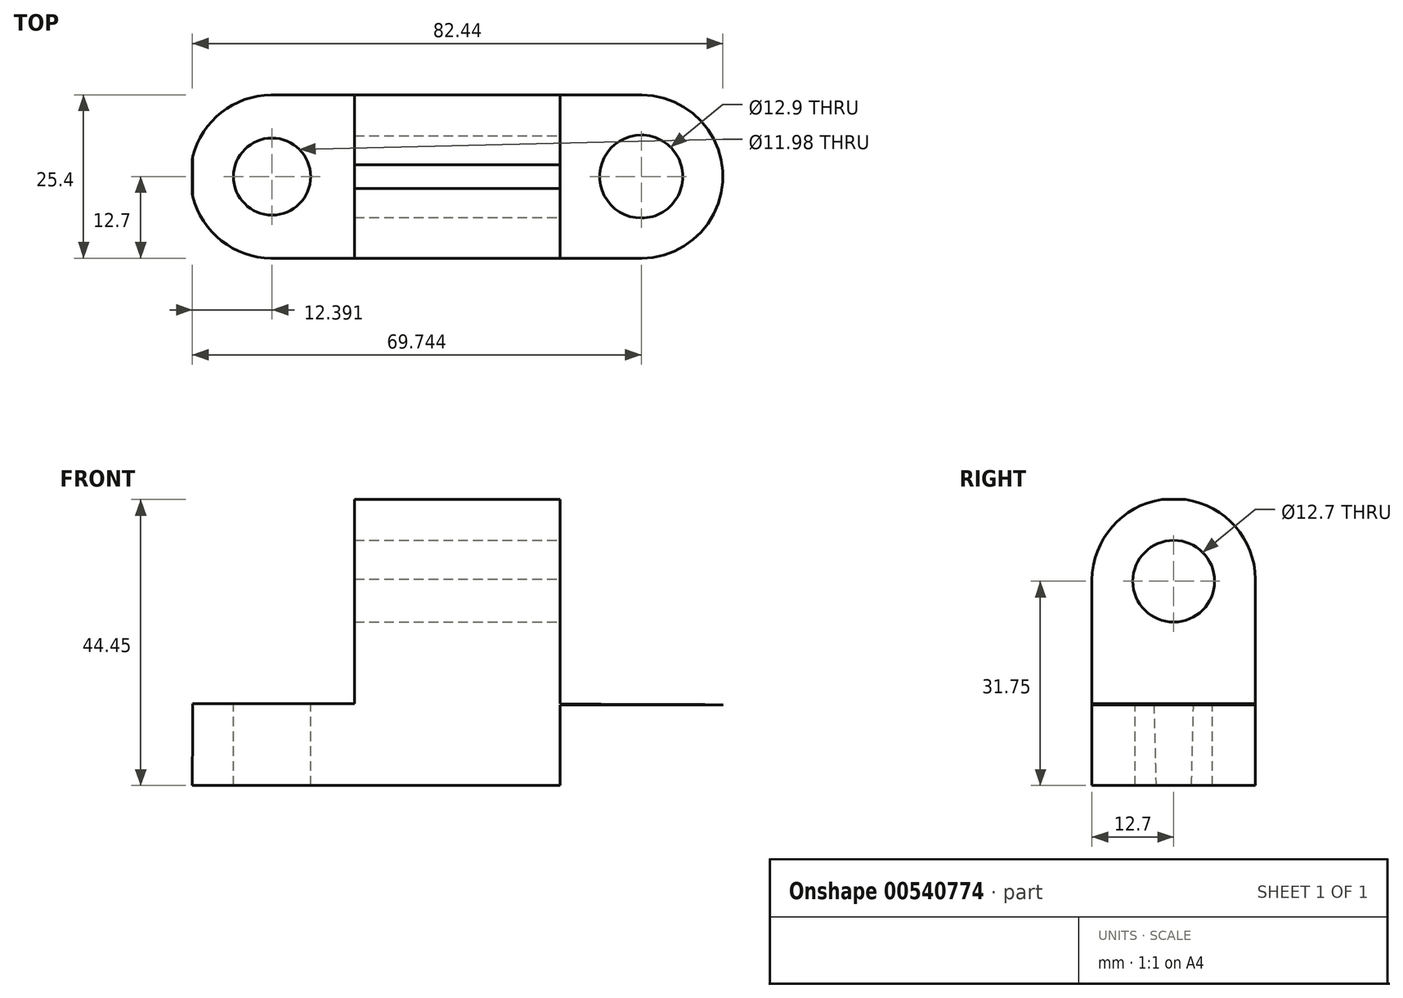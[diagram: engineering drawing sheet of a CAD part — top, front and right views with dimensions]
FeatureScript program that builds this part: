
annotation { "Feature Type Name" : "Feature", "Feature Type Description" : "" }
export const myFeature = defineFeature(function(context is Context, id is Id, definition is map)
    precondition{}
    {
        {
            var Q0;
            Q0=qCreatedBy(makeId("Front.planeOp"),FACE);
            var sketch = newSketch(context, id + "F0", { "sketchPlane" : qUnion([Q0])});
            skLineSegment(sketch, "E0", {"start": v(-37.24, 0) * mm, "end": v(45.57, 0) * mm});
            skLineSegment(sketch, "E1", {"start": v(45.57, 0) * mm, "end": v(45.57, 44.45) * mm});
            skLineSegment(sketch, "E2", {"start": v(45.57, 44.45) * mm, "end": v(-36.98, 44.45) * mm});
            skLineSegment(sketch, "E3", {"start": v(-36.98, 44.45) * mm, "end": v(-37.24, 0) * mm});
            skSolve(sketch);
        }
        {
            var Q0;
            Q0=makeQuery(id+"F0.imprint","IMPRINT",FACE,{"disambiguationData":[TD([[makeQuery(id+"F0.imprint","IMPRINT",EDGE,{"derivedFrom":sQuery(id+"F0.wireOp",EDGE,"E0")}),1.0]])]});
            extrude(context, id + "F1", {"entities" : qUnion([Q0]), "depth" : 25.4 * mm, "offsetDistance" : 25.4 * mm});
        }
        {
            var Q0;
            Q0=makeQuery(id+"F1.opExtrude","CAP_FACE",FACE,{"disambiguationData":[OSD([sQuery(id+"F0.wireOp",EDGE,"E0"),sQuery(id+"F0.wireOp",EDGE,"E1"),sQuery(id+"F0.wireOp",EDGE,"E2"),sQuery(id+"F0.wireOp",EDGE,"E3")])],"isStart":false});
            var sketch = newSketch(context, id + "F2", { "sketchPlane" : qUnion([Q0])});
            skLineSegment(sketch, "E4", {"start": v(45.57, 12.55) * mm, "end": v(20.17, 12.7) * mm});
            skLineSegment(sketch, "E5", {"start": v(20.17, 12.7) * mm, "end": v(20.17, 44.45) * mm});
            skLineSegment(sketch, "E6", {"start": v(-11.76, 12.7) * mm, "end": v(-11.76, 44.45) * mm});
            skLineSegment(sketch, "E7", {"start": v(20.17, 44.45) * mm, "end": v(45.57, 44.45) * mm});
            skLineSegment(sketch, "E8", {"start": v(45.57, 44.45) * mm, "end": v(45.57, 12.55) * mm});
            skLineSegment(sketch, "E9", {"start": v(-11.76, 44.45) * mm, "end": v(-36.98, 44.45) * mm});
            skLineSegment(sketch, "E10", {"start": v(-11.76, 12.7) * mm, "end": v(-37.16, 12.7) * mm});
            skLineSegment(sketch, "E11", {"start": v(-37.16, 12.7) * mm, "end": v(-36.98, 44.45) * mm});
            skSolve(sketch);
        }
        {
            var Q0;
            Q0=makeQuery(id+"F2.imprint","IMPRINT",FACE,{"disambiguationData":[TD([[makeQuery(id+"F2.imprint","IMPRINT",EDGE,{"derivedFrom":sQuery(id+"F2.wireOp",EDGE,"E6")}),1.0]])]});
            var Q1;
            Q1=makeQuery(id+"F2.imprint","IMPRINT",FACE,{"disambiguationData":[TD([[makeQuery(id+"F2.imprint","IMPRINT",EDGE,{"derivedFrom":sQuery(id+"F2.wireOp",EDGE,"E4")}),-1.0]])]});
            extrude(context, id + "F3", {"entities" : qUnion([Q0, Q1]), "operationType" : NewBodyOperationType.REMOVE, "oppositeDirection" : true, "depth" : 25.4 * mm, "offsetDistance" : 25.4 * mm});
        }
        {
            var Q0;
            Q0=makeQuery(id+"F3.boolean.opBoolean","COPY",FACE,{"derivedFrom":makeQuery(id+"F3.opExtrude","SWEPT_FACE",FACE,{"disambiguationData":[OSD([sQuery(id+"F2.wireOp",EDGE,"E5")])]})});
            var sketch = newSketch(context, id + "F4", { "sketchPlane" : qUnion([Q0])});
            skCircle(sketch, "E12", {"center": v(-12.7, 31.75) * mm, "radius": 6.35 * mm});
            skArc(sketch, "E13", {"start": v(0, 32.06) * mm, "mid": v(-12.83, 44.58) * mm, "end": v(-25.4, 31.8) * mm});
            skLineSegment(sketch, "E14", {"start": v(-25.4, 31.8) * mm, "end": v(-25.4, 44.45) * mm});
            skLineSegment(sketch, "E15", {"start": v(-25.4, 44.45) * mm, "end": v(0, 44.45) * mm});
            skLineSegment(sketch, "E16", {"start": v(0, 44.45) * mm, "end": v(0, 32.06) * mm});
            skSolve(sketch);
        }
        {
            var Q0;
            Q0=makeQuery(id+"F4.imprint","IMPRINT",FACE,{"disambiguationData":[TD([[makeQuery(id+"F4.imprint","IMPRINT",EDGE,{"derivedFrom":sQuery(id+"F4.wireOp",EDGE,"E12")}),1.0]])]});
            var Q1;
            {var subQ0=sQuery(id+"F4.wireOp",EDGE,"E14");var subQ1=sQuery(id+"F4.wireOp",EDGE,"E13");var subQ2=makeQuery(id+"F4.imprint","INTERSECT",VERTEX,{"derivedFrom":[subQ1,subQ0]});Q1=makeQuery(id+"F4.imprint","IMPRINT",FACE,{"disambiguationData":[TD([[makeQuery(id+"F4.imprint","IMPRINT",EDGE,{"disambiguationData":[TD([[subQ2,1.0]])],"derivedFrom":subQ1}),-1.0]])]});}
            var Q2;
            {var subQ0=sQuery(id+"F4.wireOp",EDGE,"E16");Q2=makeQuery(id+"F4.imprint","IMPRINT",FACE,{"disambiguationData":[TD([[makeQuery(id+"F4.imprint","IMPRINT",EDGE,{"derivedFrom":subQ0}),1.0]])]});}
            extrude(context, id + "F5", {"entities" : qUnion([Q0, Q1, Q2]), "operationType" : NewBodyOperationType.REMOVE, "oppositeDirection" : true, "depth" : 38.1 * mm, "offsetDistance" : 25.4 * mm});
        }
        {
            var Q0;
            Q0=makeQuery(id+"F3.boolean.opBoolean","COPY",FACE,{"derivedFrom":makeQuery(id+"F3.opExtrude","SWEPT_FACE",FACE,{"disambiguationData":[OSD([sQuery(id+"F2.wireOp",EDGE,"E4")])]})});
            var sketch = newSketch(context, id + "F6", { "sketchPlane" : qUnion([Q0])});
            skArc(sketch, "E17", {"start": v(32.8, -25.4) * mm, "mid": v(45.4, -12.7) * mm, "end": v(32.8, 0) * mm});
            skLineSegment(sketch, "E18", {"start": v(32.8, 0) * mm, "end": v(45.5, 0) * mm});
            skLineSegment(sketch, "E19", {"start": v(45.5, 0) * mm, "end": v(45.5, -25.4) * mm});
            skLineSegment(sketch, "E20", {"start": v(45.5, -25.4) * mm, "end": v(32.8, -25.4) * mm});
            skCircle(sketch, "E21", {"center": v(32.69, -12.7) * mm, "radius": 6.45 * mm});
            skSolve(sketch);
        }
        {
            var Q0;
            Q0=makeQuery(id+"F6.imprint","IMPRINT",FACE,{"disambiguationData":[TD([[makeQuery(id+"F6.imprint","IMPRINT",EDGE,{"derivedFrom":sQuery(id+"F6.wireOp",EDGE,"E17")}),-1.0]])]});
            var Q1;
            Q1=makeQuery(id+"F6.imprint","IMPRINT",FACE,{"disambiguationData":[TD([[makeQuery(id+"F6.imprint","IMPRINT",EDGE,{"derivedFrom":sQuery(id+"F6.wireOp",EDGE,"E21")}),1.0]])]});
            extrude(context, id + "F7", {"entities" : qUnion([Q0, Q1]), "operationType" : NewBodyOperationType.REMOVE, "oppositeDirection" : true, "depth" : 12.7 * mm, "offsetDistance" : 25.4 * mm});
        }
        {
            var Q0;
            Q0=makeQuery(id+"F1.opExtrude","SWEPT_FACE",FACE,{"disambiguationData":[OSD([sQuery(id+"F0.wireOp",EDGE,"E1")])]});
            extrude(context, id + "F8", {"entities" : qUnion([Q0]), "operationType" : NewBodyOperationType.REMOVE, "oppositeDirection" : true, "depth" : 25.4 * mm, "offsetDistance" : 25.4 * mm});
        }
        {
            var Q0;
            Q0=makeQuery(id+"F3.boolean.opBoolean","COPY",FACE,{"derivedFrom":makeQuery(id+"F3.opExtrude","SWEPT_FACE",FACE,{"disambiguationData":[OSD([sQuery(id+"F2.wireOp",EDGE,"E10")])]})});
            var sketch = newSketch(context, id + "F9", { "sketchPlane" : qUnion([Q0])});
            skArc(sketch, "E22", {"start": v(-24.46, 0) * mm, "mid": v(-37.29, -12.7) * mm, "end": v(-24.46, -25.4) * mm});
            skCircle(sketch, "E23", {"center": v(-24.59, -12.7) * mm, "radius": 5.99 * mm});
            skLineSegment(sketch, "E24", {"start": v(-24.46, 0) * mm, "end": v(-37.16, 0) * mm});
            skLineSegment(sketch, "E25", {"start": v(-37.16, 0) * mm, "end": v(-37.16, -25.4) * mm});
            skLineSegment(sketch, "E26", {"start": v(-37.16, -25.4) * mm, "end": v(-24.46, -25.4) * mm});
            skSolve(sketch);
        }
        {
            var Q0;
            {var subQ0=sQuery(id+"F9.wireOp",EDGE,"E24");var subQ1=sQuery(id+"F9.wireOp",EDGE,"E22");var subQ2=makeQuery(id+"F9.imprint","INTERSECT",VERTEX,{"derivedFrom":[subQ1,subQ0]});Q0=makeQuery(id+"F9.imprint","IMPRINT",FACE,{"disambiguationData":[TD([[makeQuery(id+"F9.imprint","IMPRINT",EDGE,{"disambiguationData":[TD([[subQ2,-1.0]])],"derivedFrom":subQ1}),-1.0]])]});}
            var Q1;
            Q1=makeQuery(id+"F9.imprint","IMPRINT",FACE,{"disambiguationData":[TD([[makeQuery(id+"F9.imprint","IMPRINT",EDGE,{"derivedFrom":sQuery(id+"F9.wireOp",EDGE,"E23")}),1.0]])]});
            var Q2;
            {var subQ0=sQuery(id+"F9.wireOp",EDGE,"E25");var subQ1=sQuery(id+"F9.wireOp",EDGE,"E22");var subQ2=makeQuery(id+"F9.imprint","INTERSECT",VERTEX,{"disambiguationData":[OD(1.0)],"derivedFrom":[subQ1,subQ0]});Q2=makeQuery(id+"F9.imprint","IMPRINT",FACE,{"disambiguationData":[TD([[makeQuery(id+"F9.imprint","IMPRINT",EDGE,{"disambiguationData":[TD([[subQ2,-1.0]])],"derivedFrom":subQ1}),-1.0]])]});}
            extrude(context, id + "F10", {"entities" : qUnion([Q0, Q1, Q2]), "operationType" : NewBodyOperationType.REMOVE, "oppositeDirection" : true, "depth" : 12.7 * mm, "offsetDistance" : 25.4 * mm});
        }
        {
            var Q0;
            Q0=makeQuery(id+"F1.opExtrude","SWEPT_FACE",FACE,{"disambiguationData":[OSD([sQuery(id+"F0.wireOp",EDGE,"E3")])]});
            extrude(context, id + "F11", {"entities" : qUnion([Q0]), "operationType" : NewBodyOperationType.REMOVE, "oppositeDirection" : true, "depth" : 0.25 * mm, "offsetDistance" : 25.4 * mm});
        }
    });
